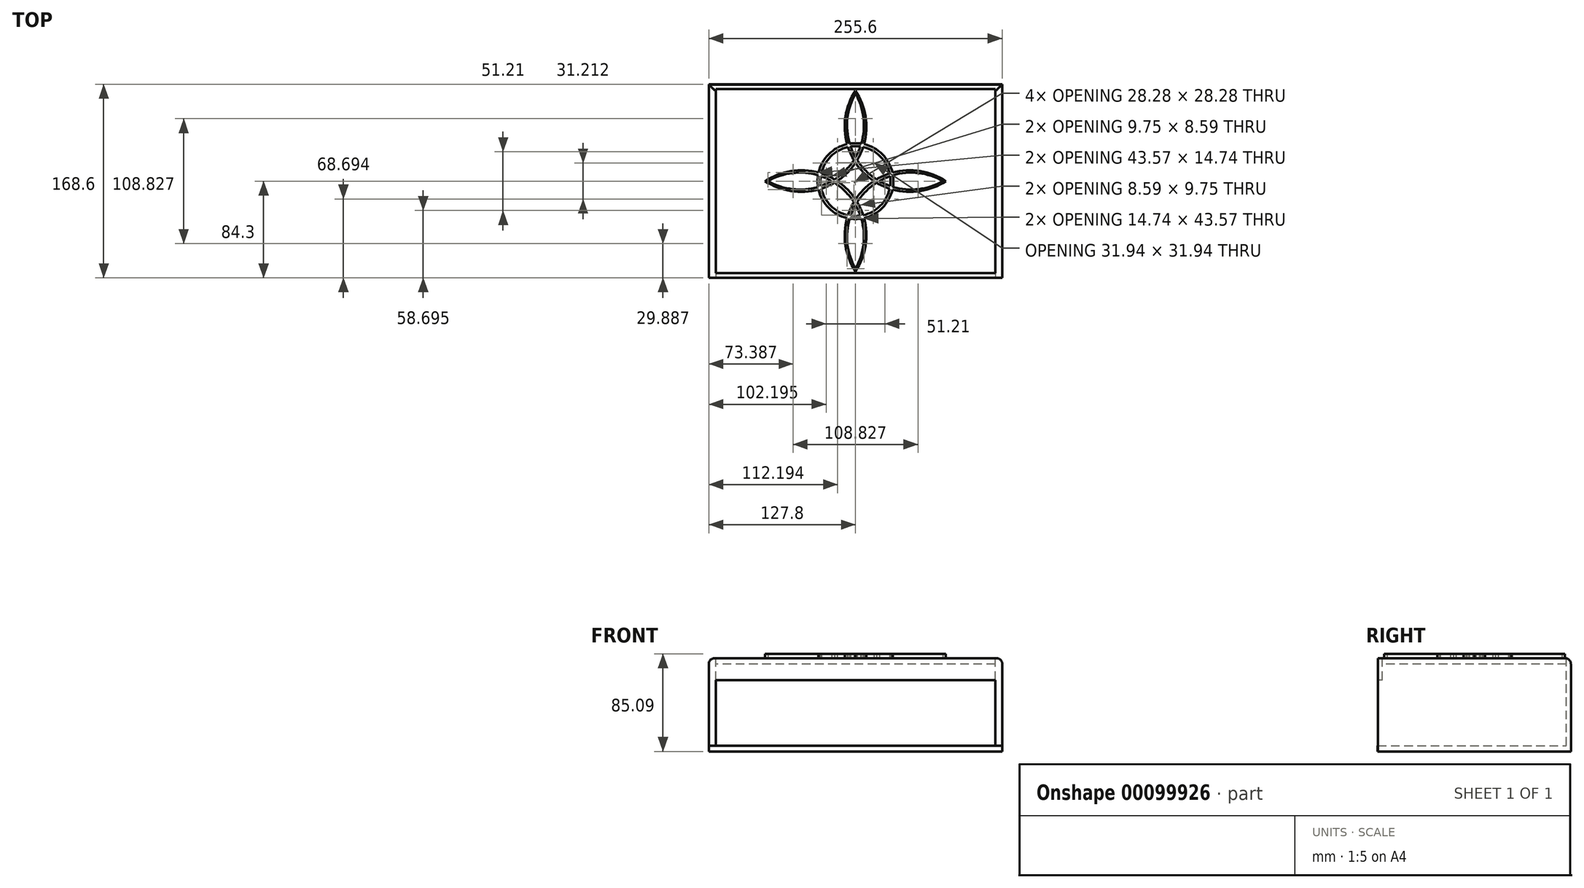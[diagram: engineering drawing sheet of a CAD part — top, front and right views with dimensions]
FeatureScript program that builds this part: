
annotation { "Feature Type Name" : "Feature", "Feature Type Description" : "" }
export const myFeature = defineFeature(function(context is Context, id is Id, definition is map)
    precondition{}
    {
        {
            var Q0;
            Q0=qCreatedBy(makeId("Top.planeOp"),FACE);
            var sketch = newSketch(context, id + "F0", { "sketchPlane" : qUnion([Q0])});
            skPoint(sketch, "E0", {"position": v(0, 0) * mm});
            skPoint(sketch, "E1", {"position": v(0, 76.2) * mm});
            skPoint(sketch, "E2", {"position": v(0, -76.2) * mm});
            skPoint(sketch, "E3", {"position": v(76.2, 0) * mm});
            skPoint(sketch, "E4", {"position": v(-76.2, 0) * mm});
            skLineSegment(sketch, "E5.bottom", {"start": v(76.2, 76.2) * mm, "end": v(-76.2, 76.2) * mm, "construction": true});
            skLineSegment(sketch, "E5.top", {"start": v(76.2, -76.2) * mm, "end": v(-76.2, -76.2) * mm, "construction": true});
            skLineSegment(sketch, "E5.left", {"start": v(76.2, 76.2) * mm, "end": v(76.2, -76.2) * mm, "construction": true});
            skLineSegment(sketch, "E5.right", {"start": v(-76.2, 76.2) * mm, "end": v(-76.2, -76.2) * mm, "construction": true});
            skPoint(sketch, "E6", {"position": v(-76.2, 76.2) * mm});
            skPoint(sketch, "E7", {"position": v(76.2, 76.2) * mm});
            skPoint(sketch, "E8", {"position": v(76.2, -76.2) * mm});
            skPoint(sketch, "E9", {"position": v(-76.2, -76.2) * mm});
            skLineSegment(sketch, "E10", {"start": v(76.2, 76.2) * mm, "end": v(-76.2, -76.2) * mm, "construction": true});
            skLineSegment(sketch, "E11", {"start": v(-76.2, 76.2) * mm, "end": v(76.2, -76.2) * mm, "construction": true});
            skLineSegment(sketch, "E12", {"start": v(0, 76.2) * mm, "end": v(0, -76.2) * mm, "construction": true});
            skLineSegment(sketch, "E13", {"start": v(-76.2, 0) * mm, "end": v(76.2, 0) * mm, "construction": true});
            skPoint(sketch, "E14", {"position": v(8.98, 8.98) * mm});
            skPoint(sketch, "E15", {"position": v(-8.98, -8.98) * mm});
            skPoint(sketch, "E16", {"position": v(8.98, -8.98) * mm});
            skPoint(sketch, "E17", {"position": v(-8.98, 8.98) * mm});
            skArc(sketch, "E18", {"start": v(0, 76.2) * mm, "mid": v(8.98, 8.98) * mm, "end": v(76.2, 0) * mm});
            skArc(sketch, "E19", {"start": v(-76.2, 0) * mm, "mid": v(-8.98, 8.98) * mm, "end": v(0, 76.2) * mm});
            skArc(sketch, "E20", {"start": v(0, -76.2) * mm, "mid": v(-8.98, -8.98) * mm, "end": v(-76.2, 0) * mm});
            skArc(sketch, "E21", {"start": v(76.2, 0) * mm, "mid": v(8.98, -8.98) * mm, "end": v(0, -76.2) * mm});
            skPoint(sketch, "E22", {"position": v(7.18, -7.18) * mm});
            skPoint(sketch, "E23", {"position": v(-7.18, 7.18) * mm});
            skPoint(sketch, "E24", {"position": v(7.18, 7.18) * mm});
            skPoint(sketch, "E25", {"position": v(-7.18, -7.18) * mm});
            skPoint(sketch, "E26", {"position": v(0, 78.74) * mm});
            skPoint(sketch, "E27", {"position": v(-78.74, 0) * mm});
            skPoint(sketch, "E28", {"position": v(0, -78.74) * mm});
            skPoint(sketch, "E29", {"position": v(78.74, 0) * mm});
            skArc(sketch, "E30", {"start": v(-78.74, 0) * mm, "mid": v(-7.18, 7.18) * mm, "end": v(0, 78.74) * mm});
            skArc(sketch, "E31", {"start": v(0, -78.74) * mm, "mid": v(-7.18, -7.18) * mm, "end": v(-78.74, 0) * mm});
            skArc(sketch, "E32", {"start": v(78.74, 0) * mm, "mid": v(7.18, -7.18) * mm, "end": v(0, -78.74) * mm});
            skArc(sketch, "E33", {"start": v(0, 78.74) * mm, "mid": v(7.18, 7.18) * mm, "end": v(78.74, 0) * mm});
            skPoint(sketch, "E34", {"position": v(0, 30.48) * mm});
            skPoint(sketch, "E35", {"position": v(0, 33.02) * mm});
            skCircle(sketch, "E36", {"center": v(0, 0) * mm, "radius": 30.48 * mm});
            skCircle(sketch, "E37", {"center": v(0, 0) * mm, "radius": 33.02 * mm});
            skSolve(sketch);
        }
        {
            var Q0;
            {var subQ0=sQuery(id+"F0.wireOp",EDGE,"E37");var subQ1=sQuery(id+"F0.wireOp",EDGE,"E31");var subQ2=makeQuery(id+"F0.imprint","INTERSECT",VERTEX,{"disambiguationData":[OD(0.0)],"derivedFrom":[subQ1,subQ0]});Q0=makeQuery(id+"F0.imprint","IMPRINT",FACE,{"disambiguationData":[TD([[makeQuery(id+"F0.imprint","IMPRINT",EDGE,{"disambiguationData":[TD([[subQ2,-1.0]])],"derivedFrom":subQ1}),-1.0]])]});}
            var Q1;
            {var subQ0=sQuery(id+"F0.wireOp",EDGE,"E36");var subQ1=sQuery(id+"F0.wireOp",EDGE,"E18");var subQ2=makeQuery(id+"F0.imprint","INTERSECT",VERTEX,{"disambiguationData":[OD(1.0)],"derivedFrom":[subQ1,subQ0]});Q1=makeQuery(id+"F0.imprint","IMPRINT",FACE,{"disambiguationData":[TD([[makeQuery(id+"F0.imprint","IMPRINT",EDGE,{"disambiguationData":[TD([[subQ2,-1.0]])],"derivedFrom":subQ1}),-1.0]])]});}
            var Q2;
            {var subQ0=sQuery(id+"F0.wireOp",EDGE,"E36");var subQ1=sQuery(id+"F0.wireOp",EDGE,"E18");var subQ2=makeQuery(id+"F0.imprint","INTERSECT",VERTEX,{"disambiguationData":[OD(1.0)],"derivedFrom":[subQ1,subQ0]});Q2=makeQuery(id+"F0.imprint","IMPRINT",FACE,{"disambiguationData":[TD([[makeQuery(id+"F0.imprint","IMPRINT",EDGE,{"disambiguationData":[TD([[subQ2,-1.0]])],"derivedFrom":subQ1}),1.0]])]});}
            var Q3;
            {var subQ6=sQuery(id+"F0.wireOp",EDGE,"E21");var subQ7=sQuery(id+"F0.wireOp",EDGE,"E18");var subQ8=makeQuery(id+"F0.imprint","INTERSECT",VERTEX,{"disambiguationData":[OD(0.0)],"derivedFrom":[subQ7,subQ6]});Q3=makeQuery(id+"F0.imprint","IMPRINT",FACE,{"disambiguationData":[TD([[makeQuery(id+"F0.imprint","IMPRINT",EDGE,{"disambiguationData":[TD([[subQ8,1.0]])],"derivedFrom":subQ7}),-1.0]])]});}
            var Q4;
            {var subQ0=sQuery(id+"F0.wireOp",EDGE,"E21");var subQ1=sQuery(id+"F0.wireOp",EDGE,"E18");var subQ2=makeQuery(id+"F0.imprint","INTERSECT",VERTEX,{"disambiguationData":[OD(1.0)],"derivedFrom":[subQ1,subQ0]});Q4=makeQuery(id+"F0.imprint","IMPRINT",FACE,{"disambiguationData":[TD([[makeQuery(id+"F0.imprint","IMPRINT",EDGE,{"disambiguationData":[TD([[subQ2,-1.0]])],"derivedFrom":subQ1}),-1.0]])]});}
            var Q5;
            {var subQ0=sQuery(id+"F0.wireOp",EDGE,"E32");var subQ1=sQuery(id+"F0.wireOp",EDGE,"E18");var subQ2=makeQuery(id+"F0.imprint","INTERSECT",VERTEX,{"derivedFrom":[subQ1,subQ0]});Q5=makeQuery(id+"F0.imprint","IMPRINT",FACE,{"disambiguationData":[TD([[makeQuery(id+"F0.imprint","IMPRINT",EDGE,{"disambiguationData":[TD([[subQ2,-1.0]])],"derivedFrom":subQ1}),1.0]])]});}
            var Q6;
            {var subQ0=sQuery(id+"F0.wireOp",EDGE,"E37");var subQ1=sQuery(id+"F0.wireOp",EDGE,"E30");var subQ2=makeQuery(id+"F0.imprint","INTERSECT",VERTEX,{"disambiguationData":[OD(1.0)],"derivedFrom":[subQ1,subQ0]});Q6=makeQuery(id+"F0.imprint","IMPRINT",FACE,{"disambiguationData":[TD([[makeQuery(id+"F0.imprint","IMPRINT",EDGE,{"disambiguationData":[TD([[subQ2,1.0]])],"derivedFrom":subQ1}),-1.0]])]});}
            var Q7;
            {var subQ0=sQuery(id+"F0.wireOp",EDGE,"E37");var subQ1=sQuery(id+"F0.wireOp",EDGE,"E21");var subQ2=makeQuery(id+"F0.imprint","INTERSECT",VERTEX,{"disambiguationData":[OD(0.0)],"derivedFrom":[subQ1,subQ0]});Q7=makeQuery(id+"F0.imprint","IMPRINT",FACE,{"disambiguationData":[TD([[makeQuery(id+"F0.imprint","IMPRINT",EDGE,{"disambiguationData":[TD([[subQ2,-1.0]])],"derivedFrom":subQ1}),-1.0]])]});}
            var Q8;
            {var subQ0=sQuery(id+"F0.wireOp",EDGE,"E36");var subQ1=sQuery(id+"F0.wireOp",EDGE,"E20");var subQ2=makeQuery(id+"F0.imprint","INTERSECT",VERTEX,{"disambiguationData":[OD(0.0)],"derivedFrom":[subQ1,subQ0]});Q8=makeQuery(id+"F0.imprint","IMPRINT",FACE,{"disambiguationData":[TD([[makeQuery(id+"F0.imprint","IMPRINT",EDGE,{"disambiguationData":[TD([[subQ2,-1.0]])],"derivedFrom":subQ1}),-1.0]])]});}
            var Q9;
            {var subQ6=sQuery(id+"F0.wireOp",EDGE,"E20");var subQ8=sQuery(id+"F0.wireOp",EDGE,"E21");var subQ9=makeQuery(id+"F0.imprint","INTERSECT",VERTEX,{"disambiguationData":[OD(0.0)],"derivedFrom":[subQ6,subQ8]});Q9=makeQuery(id+"F0.imprint","IMPRINT",FACE,{"disambiguationData":[TD([[makeQuery(id+"F0.imprint","IMPRINT",EDGE,{"disambiguationData":[TD([[subQ9,-1.0]])],"derivedFrom":subQ6}),-1.0]])]});}
            var Q10;
            {var subQ0=sQuery(id+"F0.wireOp",EDGE,"E37");var subQ1=sQuery(id+"F0.wireOp",EDGE,"E20");var subQ2=makeQuery(id+"F0.imprint","INTERSECT",VERTEX,{"disambiguationData":[OD(0.0)],"derivedFrom":[subQ1,subQ0]});Q10=makeQuery(id+"F0.imprint","IMPRINT",FACE,{"disambiguationData":[TD([[makeQuery(id+"F0.imprint","IMPRINT",EDGE,{"disambiguationData":[TD([[subQ2,-1.0]])],"derivedFrom":subQ1}),1.0]])]});}
            var Q11;
            {var subQ0=sQuery(id+"F0.wireOp",EDGE,"E37");var subQ1=sQuery(id+"F0.wireOp",EDGE,"E20");var subQ2=makeQuery(id+"F0.imprint","INTERSECT",VERTEX,{"disambiguationData":[OD(0.0)],"derivedFrom":[subQ1,subQ0]});Q11=makeQuery(id+"F0.imprint","IMPRINT",FACE,{"disambiguationData":[TD([[makeQuery(id+"F0.imprint","IMPRINT",EDGE,{"disambiguationData":[TD([[subQ2,-1.0]])],"derivedFrom":subQ1}),-1.0]])]});}
            var Q12;
            {var subQ0=sQuery(id+"F0.wireOp",EDGE,"E36");var subQ1=sQuery(id+"F0.wireOp",EDGE,"E21");var subQ2=makeQuery(id+"F0.imprint","INTERSECT",VERTEX,{"disambiguationData":[OD(1.0)],"derivedFrom":[subQ1,subQ0]});Q12=makeQuery(id+"F0.imprint","IMPRINT",FACE,{"disambiguationData":[TD([[makeQuery(id+"F0.imprint","IMPRINT",EDGE,{"disambiguationData":[TD([[subQ2,-1.0]])],"derivedFrom":subQ1}),-1.0]])]});}
            var Q13;
            {var subQ0=sQuery(id+"F0.wireOp",EDGE,"E21");var subQ1=sQuery(id+"F0.wireOp",EDGE,"E20");var subQ2=makeQuery(id+"F0.imprint","INTERSECT",VERTEX,{"disambiguationData":[OD(1.0)],"derivedFrom":[subQ1,subQ0]});Q13=makeQuery(id+"F0.imprint","IMPRINT",FACE,{"disambiguationData":[TD([[makeQuery(id+"F0.imprint","IMPRINT",EDGE,{"disambiguationData":[TD([[subQ2,-1.0]])],"derivedFrom":subQ1}),1.0]])]});}
            var Q14;
            {var subQ0=sQuery(id+"F0.wireOp",EDGE,"E33");var subQ1=sQuery(id+"F0.wireOp",EDGE,"E21");var subQ2=makeQuery(id+"F0.imprint","INTERSECT",VERTEX,{"derivedFrom":[subQ1,subQ0]});Q14=makeQuery(id+"F0.imprint","IMPRINT",FACE,{"disambiguationData":[TD([[makeQuery(id+"F0.imprint","IMPRINT",EDGE,{"disambiguationData":[TD([[subQ2,-1.0]])],"derivedFrom":subQ1}),-1.0]])]});}
            var Q15;
            {var subQ0=sQuery(id+"F0.wireOp",EDGE,"E30");var subQ1=sQuery(id+"F0.wireOp",EDGE,"E18");var subQ2=makeQuery(id+"F0.imprint","INTERSECT",VERTEX,{"derivedFrom":[subQ1,subQ0]});Q15=makeQuery(id+"F0.imprint","IMPRINT",FACE,{"disambiguationData":[TD([[makeQuery(id+"F0.imprint","IMPRINT",EDGE,{"disambiguationData":[TD([[subQ2,-1.0]])],"derivedFrom":subQ1}),-1.0]])]});}
            var Q16;
            {var subQ0=sQuery(id+"F0.wireOp",EDGE,"E31");var subQ1=sQuery(id+"F0.wireOp",EDGE,"E19");var subQ2=makeQuery(id+"F0.imprint","INTERSECT",VERTEX,{"derivedFrom":[subQ1,subQ0]});Q16=makeQuery(id+"F0.imprint","IMPRINT",FACE,{"disambiguationData":[TD([[makeQuery(id+"F0.imprint","IMPRINT",EDGE,{"disambiguationData":[TD([[subQ2,-1.0]])],"derivedFrom":subQ1}),-1.0]])]});}
            var Q17;
            {var subQ0=sQuery(id+"F0.wireOp",EDGE,"E32");var subQ1=sQuery(id+"F0.wireOp",EDGE,"E20");var subQ2=makeQuery(id+"F0.imprint","INTERSECT",VERTEX,{"derivedFrom":[subQ1,subQ0]});Q17=makeQuery(id+"F0.imprint","IMPRINT",FACE,{"disambiguationData":[TD([[makeQuery(id+"F0.imprint","IMPRINT",EDGE,{"disambiguationData":[TD([[subQ2,-1.0]])],"derivedFrom":subQ1}),-1.0]])]});}
            var Q18;
            {var subQ0=sQuery(id+"F0.wireOp",EDGE,"E20");var subQ1=sQuery(id+"F0.wireOp",EDGE,"E19");var subQ2=makeQuery(id+"F0.imprint","INTERSECT",VERTEX,{"disambiguationData":[OD(1.0)],"derivedFrom":[subQ1,subQ0]});Q18=makeQuery(id+"F0.imprint","IMPRINT",FACE,{"disambiguationData":[TD([[makeQuery(id+"F0.imprint","IMPRINT",EDGE,{"disambiguationData":[TD([[subQ2,-1.0]])],"derivedFrom":subQ1}),1.0]])]});}
            var Q19;
            {var subQ0=sQuery(id+"F0.wireOp",EDGE,"E36");var subQ1=sQuery(id+"F0.wireOp",EDGE,"E19");var subQ2=makeQuery(id+"F0.imprint","INTERSECT",VERTEX,{"disambiguationData":[OD(0.0)],"derivedFrom":[subQ1,subQ0]});Q19=makeQuery(id+"F0.imprint","IMPRINT",FACE,{"disambiguationData":[TD([[makeQuery(id+"F0.imprint","IMPRINT",EDGE,{"disambiguationData":[TD([[subQ2,-1.0]])],"derivedFrom":subQ1}),-1.0]])]});}
            var Q20;
            {var subQ0=sQuery(id+"F0.wireOp",EDGE,"E37");var subQ1=sQuery(id+"F0.wireOp",EDGE,"E19");var subQ2=makeQuery(id+"F0.imprint","INTERSECT",VERTEX,{"disambiguationData":[OD(0.0)],"derivedFrom":[subQ1,subQ0]});Q20=makeQuery(id+"F0.imprint","IMPRINT",FACE,{"disambiguationData":[TD([[makeQuery(id+"F0.imprint","IMPRINT",EDGE,{"disambiguationData":[TD([[subQ2,-1.0]])],"derivedFrom":subQ1}),1.0]])]});}
            var Q21;
            {var subQ0=sQuery(id+"F0.wireOp",EDGE,"E37");var subQ1=sQuery(id+"F0.wireOp",EDGE,"E19");var subQ2=makeQuery(id+"F0.imprint","INTERSECT",VERTEX,{"disambiguationData":[OD(0.0)],"derivedFrom":[subQ1,subQ0]});Q21=makeQuery(id+"F0.imprint","IMPRINT",FACE,{"disambiguationData":[TD([[makeQuery(id+"F0.imprint","IMPRINT",EDGE,{"disambiguationData":[TD([[subQ2,-1.0]])],"derivedFrom":subQ1}),-1.0]])]});}
            var Q22;
            {var subQ0=sQuery(id+"F0.wireOp",EDGE,"E37");var subQ1=sQuery(id+"F0.wireOp",EDGE,"E30");var subQ2=makeQuery(id+"F0.imprint","INTERSECT",VERTEX,{"disambiguationData":[OD(0.0)],"derivedFrom":[subQ1,subQ0]});Q22=makeQuery(id+"F0.imprint","IMPRINT",FACE,{"disambiguationData":[TD([[makeQuery(id+"F0.imprint","IMPRINT",EDGE,{"disambiguationData":[TD([[subQ2,-1.0]])],"derivedFrom":subQ1}),-1.0]])]});}
            var Q23;
            {var subQ0=sQuery(id+"F0.wireOp",EDGE,"E36");var subQ1=sQuery(id+"F0.wireOp",EDGE,"E20");var subQ2=makeQuery(id+"F0.imprint","INTERSECT",VERTEX,{"disambiguationData":[OD(1.0)],"derivedFrom":[subQ1,subQ0]});Q23=makeQuery(id+"F0.imprint","IMPRINT",FACE,{"disambiguationData":[TD([[makeQuery(id+"F0.imprint","IMPRINT",EDGE,{"disambiguationData":[TD([[subQ2,-1.0]])],"derivedFrom":subQ1}),-1.0]])]});}
            var Q24;
            {var subQ6=sQuery(id+"F0.wireOp",EDGE,"E20");var subQ7=sQuery(id+"F0.wireOp",EDGE,"E19");var subQ8=makeQuery(id+"F0.imprint","INTERSECT",VERTEX,{"disambiguationData":[OD(0.0)],"derivedFrom":[subQ7,subQ6]});Q24=makeQuery(id+"F0.imprint","IMPRINT",FACE,{"disambiguationData":[TD([[makeQuery(id+"F0.imprint","IMPRINT",EDGE,{"disambiguationData":[TD([[subQ8,-1.0]])],"derivedFrom":subQ7}),-1.0]])]});}
            var Q25;
            {var subQ0=sQuery(id+"F0.wireOp",EDGE,"E37");var subQ1=sQuery(id+"F0.wireOp",EDGE,"E31");var subQ2=makeQuery(id+"F0.imprint","INTERSECT",VERTEX,{"disambiguationData":[OD(1.0)],"derivedFrom":[subQ1,subQ0]});Q25=makeQuery(id+"F0.imprint","IMPRINT",FACE,{"disambiguationData":[TD([[makeQuery(id+"F0.imprint","IMPRINT",EDGE,{"disambiguationData":[TD([[subQ2,1.0]])],"derivedFrom":subQ1}),-1.0]])]});}
            var Q26;
            {var subQ0=sQuery(id+"F0.wireOp",EDGE,"E36");var subQ1=sQuery(id+"F0.wireOp",EDGE,"E18");var subQ2=makeQuery(id+"F0.imprint","INTERSECT",VERTEX,{"disambiguationData":[OD(0.0)],"derivedFrom":[subQ1,subQ0]});Q26=makeQuery(id+"F0.imprint","IMPRINT",FACE,{"disambiguationData":[TD([[makeQuery(id+"F0.imprint","IMPRINT",EDGE,{"disambiguationData":[TD([[subQ2,-1.0]])],"derivedFrom":subQ1}),-1.0]])]});}
            var Q27;
            {var subQ0=sQuery(id+"F0.wireOp",EDGE,"E19");var subQ1=sQuery(id+"F0.wireOp",EDGE,"E18");var subQ2=makeQuery(id+"F0.imprint","INTERSECT",VERTEX,{"disambiguationData":[OD(1.0)],"derivedFrom":[subQ1,subQ0]});Q27=makeQuery(id+"F0.imprint","IMPRINT",FACE,{"disambiguationData":[TD([[makeQuery(id+"F0.imprint","IMPRINT",EDGE,{"disambiguationData":[TD([[subQ2,-1.0]])],"derivedFrom":subQ1}),1.0]])]});}
            var Q28;
            {var subQ0=sQuery(id+"F0.wireOp",EDGE,"E37");var subQ1=sQuery(id+"F0.wireOp",EDGE,"E18");var subQ2=makeQuery(id+"F0.imprint","INTERSECT",VERTEX,{"disambiguationData":[OD(0.0)],"derivedFrom":[subQ1,subQ0]});Q28=makeQuery(id+"F0.imprint","IMPRINT",FACE,{"disambiguationData":[TD([[makeQuery(id+"F0.imprint","IMPRINT",EDGE,{"disambiguationData":[TD([[subQ2,-1.0]])],"derivedFrom":subQ1}),1.0]])]});}
            var Q29;
            {var subQ6=sQuery(id+"F0.wireOp",EDGE,"E19");var subQ7=sQuery(id+"F0.wireOp",EDGE,"E18");var subQ8=makeQuery(id+"F0.imprint","INTERSECT",VERTEX,{"disambiguationData":[OD(0.0)],"derivedFrom":[subQ7,subQ6]});Q29=makeQuery(id+"F0.imprint","IMPRINT",FACE,{"disambiguationData":[TD([[makeQuery(id+"F0.imprint","IMPRINT",EDGE,{"disambiguationData":[TD([[subQ8,-1.0]])],"derivedFrom":subQ7}),-1.0]])]});}
            var Q30;
            {var subQ0=sQuery(id+"F0.wireOp",EDGE,"E36");var subQ1=sQuery(id+"F0.wireOp",EDGE,"E19");var subQ2=makeQuery(id+"F0.imprint","INTERSECT",VERTEX,{"disambiguationData":[OD(1.0)],"derivedFrom":[subQ1,subQ0]});Q30=makeQuery(id+"F0.imprint","IMPRINT",FACE,{"disambiguationData":[TD([[makeQuery(id+"F0.imprint","IMPRINT",EDGE,{"disambiguationData":[TD([[subQ2,-1.0]])],"derivedFrom":subQ1}),-1.0]])]});}
            var Q31;
            {var subQ0=sQuery(id+"F0.wireOp",EDGE,"E19");var subQ1=sQuery(id+"F0.wireOp",EDGE,"E18");var subQ2=makeQuery(id+"F0.imprint","INTERSECT",VERTEX,{"disambiguationData":[OD(1.0)],"derivedFrom":[subQ1,subQ0]});Q31=makeQuery(id+"F0.imprint","IMPRINT",FACE,{"disambiguationData":[TD([[makeQuery(id+"F0.imprint","IMPRINT",EDGE,{"disambiguationData":[TD([[subQ2,-1.0]])],"derivedFrom":subQ1}),-1.0]])]});}
            var Q32;
            {var subQ0=sQuery(id+"F0.wireOp",EDGE,"E37");var subQ1=sQuery(id+"F0.wireOp",EDGE,"E18");var subQ2=makeQuery(id+"F0.imprint","INTERSECT",VERTEX,{"disambiguationData":[OD(0.0)],"derivedFrom":[subQ1,subQ0]});Q32=makeQuery(id+"F0.imprint","IMPRINT",FACE,{"disambiguationData":[TD([[makeQuery(id+"F0.imprint","IMPRINT",EDGE,{"disambiguationData":[TD([[subQ2,-1.0]])],"derivedFrom":subQ1}),-1.0]])]});}
            var Q33;
            {var subQ0=sQuery(id+"F0.wireOp",EDGE,"E20");var subQ1=sQuery(id+"F0.wireOp",EDGE,"E19");var subQ2=makeQuery(id+"F0.imprint","INTERSECT",VERTEX,{"disambiguationData":[OD(1.0)],"derivedFrom":[subQ1,subQ0]});Q33=makeQuery(id+"F0.imprint","IMPRINT",FACE,{"disambiguationData":[TD([[makeQuery(id+"F0.imprint","IMPRINT",EDGE,{"disambiguationData":[TD([[subQ2,-1.0]])],"derivedFrom":subQ1}),-1.0]])]});}
            var Q34;
            {var subQ0=sQuery(id+"F0.wireOp",EDGE,"E21");var subQ1=sQuery(id+"F0.wireOp",EDGE,"E20");var subQ2=makeQuery(id+"F0.imprint","INTERSECT",VERTEX,{"disambiguationData":[OD(1.0)],"derivedFrom":[subQ1,subQ0]});Q34=makeQuery(id+"F0.imprint","IMPRINT",FACE,{"disambiguationData":[TD([[makeQuery(id+"F0.imprint","IMPRINT",EDGE,{"disambiguationData":[TD([[subQ2,-1.0]])],"derivedFrom":subQ1}),-1.0]])]});}
            var Q35;
            {var subQ0=sQuery(id+"F0.wireOp",EDGE,"E32");var subQ1=sQuery(id+"F0.wireOp",EDGE,"E18");var subQ2=makeQuery(id+"F0.imprint","INTERSECT",VERTEX,{"derivedFrom":[subQ1,subQ0]});Q35=makeQuery(id+"F0.imprint","IMPRINT",FACE,{"disambiguationData":[TD([[makeQuery(id+"F0.imprint","IMPRINT",EDGE,{"disambiguationData":[TD([[subQ2,-1.0]])],"derivedFrom":subQ1}),-1.0]])]});}
            extrude(context, id + "F1", {"entities" : qUnion([Q0, Q1, Q2, Q3, Q4, Q5, Q6, Q7, Q8, Q9, Q10, Q11, Q12, Q13, Q14, Q15, Q16, Q17, Q18, Q19, Q20, Q21, Q22, Q23, Q24, Q25, Q26, Q27, Q28, Q29, Q30, Q31, Q32, Q33, Q34, Q35]), "depth" : 3.8 * mm});
        }
        {
            var Q0;
            Q0=qCreatedBy(makeId("Top.planeOp"),FACE);
            var sketch = newSketch(context, id + "F2", { "sketchPlane" : qUnion([Q0])});
            skPoint(sketch, "E38", {"position": v(0, 0) * mm});
            skLineSegment(sketch, "E39.bottom", {"start": v(127.8, 84.12) * mm, "end": v(-127.8, 84.12) * mm});
            skLineSegment(sketch, "E39.top", {"start": v(127.8, -84.12) * mm, "end": v(-127.8, -84.12) * mm});
            skLineSegment(sketch, "E39.left", {"start": v(127.8, 84.12) * mm, "end": v(127.8, -84.12) * mm});
            skLineSegment(sketch, "E39.right", {"start": v(-127.8, 84.12) * mm, "end": v(-127.8, -84.12) * mm});
            skPoint(sketch, "E40", {"position": v(127.8, 84.12) * mm});
            skPoint(sketch, "E41", {"position": v(127.8, -84.12) * mm});
            skPoint(sketch, "E42", {"position": v(-127.8, -84.12) * mm});
            skPoint(sketch, "E43", {"position": v(-127.8, 84.12) * mm});
            skLineSegment(sketch, "E44", {"start": v(-127.8, -84.12) * mm, "end": v(127.8, 84.12) * mm, "construction": true});
            skLineSegment(sketch, "E45", {"start": v(-127.8, 84.12) * mm, "end": v(127.8, -84.12) * mm, "construction": true});
            skLineSegment(sketch, "E46.bottom", {"start": v(121.71, 80.12) * mm, "end": v(-121.71, 80.12) * mm});
            skLineSegment(sketch, "E46.top", {"start": v(121.71, -80.12) * mm, "end": v(-121.71, -80.12) * mm});
            skLineSegment(sketch, "E46.left", {"start": v(121.71, 80.12) * mm, "end": v(121.71, -80.12) * mm});
            skLineSegment(sketch, "E46.right", {"start": v(-121.71, 80.12) * mm, "end": v(-121.71, -80.12) * mm});
            skPoint(sketch, "E47", {"position": v(0, 80.12) * mm});
            skPoint(sketch, "E48", {"position": v(0, -80.12) * mm});
            skLineSegment(sketch, "E49", {"start": v(0, 80.12) * mm, "end": v(0, -80.12) * mm, "construction": true});
            skLineSegment(sketch, "E50", {"start": v(-121.71, -80.12) * mm, "end": v(-121.71, -84.12) * mm});
            skLineSegment(sketch, "E51", {"start": v(121.71, -80.12) * mm, "end": v(121.71, -84.12) * mm});
            skSolve(sketch);
        }
        {
            var Q0;
            Q0=makeQuery(id+"F2.imprint","IMPRINT",FACE,{"disambiguationData":[TD([[makeQuery(id+"F2.imprint","IMPRINT",EDGE,{"derivedFrom":sQuery(id+"F2.wireOp",EDGE,"E46.bottom")}),1.0]])]});
            cPlane(context, id + "F3", {"entities" : qUnion([Q0]), "cplaneType" : CPlaneType.OFFSET, "offset" : 76.2 * mm, "oppositeDirection" : true, "width" : 152.4 * mm, "height" : 152.4 * mm});
        }
        {
            var Q0;
            Q0=qCreatedBy(id+"F3.planeOp",FACE);
            var sketch = newSketch(context, id + "F4", { "sketchPlane" : qUnion([Q0])});
            skPoint(sketch, "E52", {"position": v(0, 0) * mm});
            skPoint(sketch, "E53", {"position": v(127.7, -84.3) * mm});
            skLineSegment(sketch, "E54.bottom", {"start": v(127.7, -84.3) * mm, "end": v(-127.7, -84.3) * mm});
            skLineSegment(sketch, "E54.top", {"start": v(127.7, 84.3) * mm, "end": v(-127.7, 84.3) * mm});
            skLineSegment(sketch, "E54.left", {"start": v(127.7, -84.3) * mm, "end": v(127.7, 84.3) * mm});
            skLineSegment(sketch, "E54.right", {"start": v(-127.7, -84.3) * mm, "end": v(-127.7, 84.3) * mm});
            skSolve(sketch);
        }
        {
            var Q0;
            Q0=makeQuery(id+"F2.imprint","IMPRINT",FACE,{"disambiguationData":[TD([[makeQuery(id+"F2.imprint","IMPRINT",EDGE,{"derivedFrom":sQuery(id+"F2.wireOp",EDGE,"E39.bottom")}),1.0]])]});
            extrude(context, id + "F8", {"entities" : qUnion([Q0]), "oppositeDirection" : true, "depth" : 81.28 * mm});
        }
        {
            var Q0;
            Q0=makeQuery(id+"F2.imprint","IMPRINT",FACE,{"disambiguationData":[TD([[makeQuery(id+"F2.imprint","IMPRINT",EDGE,{"derivedFrom":sQuery(id+"F2.wireOp",EDGE,"E46.top")}),1.0]])]});
            extrude(context, id + "F5", {"entities" : qUnion([Q0]), "operationType" : NewBodyOperationType.ADD, "oppositeDirection" : true, "depth" : 19.05 * mm});
        }
        {
            var Q0;
            Q0=makeQuery(id+"F2.imprint","IMPRINT",FACE,{"disambiguationData":[TD([[makeQuery(id+"F2.imprint","IMPRINT",EDGE,{"derivedFrom":sQuery(id+"F2.wireOp",EDGE,"E46.bottom")}),1.0]])]});
            extrude(context, id + "F6", {"entities" : qUnion([Q0]), "oppositeDirection" : true, "depth" : 5.08 * mm});
        }
        {
            var Q0;
            Q0=makeQuery(id+"F4.imprint","IMPRINT",FACE,{"disambiguationData":[TD([[makeQuery(id+"F4.imprint","IMPRINT",EDGE,{"derivedFrom":sQuery(id+"F4.wireOp",EDGE,"E54.bottom")}),-1.0]])]});
            extrude(context, id + "F9", {"entities" : qUnion([Q0]), "operationType" : NewBodyOperationType.ADD, "oppositeDirection" : true, "depth" : 5.08 * mm});
        }
        {
            var Q0;
            Q0=makeQuery(id+"F8.opExtrude","CAP_EDGE",EDGE,{"disambiguationData":[OSD([sQuery(id+"F2.wireOp",EDGE,"E39.left")])],"isStart":true});
            var Q1;
            Q1=makeQuery(id+"F8.opExtrude","CAP_EDGE",EDGE,{"disambiguationData":[OSD([sQuery(id+"F2.wireOp",EDGE,"E39.right")])],"isStart":true});
            var Q2;
            Q2=makeQuery(id+"F8.opExtrude","CAP_EDGE",EDGE,{"disambiguationData":[OSD([sQuery(id+"F2.wireOp",EDGE,"E39.bottom")])],"isStart":true});
            fillet(context, id + "F7", {"entities" : qUnion([Q0, Q1, Q2]), "radius" : 5.08 * mm, "tangentPropagation" : true, "allowEdgeOverflow" : false});
        }
    });
